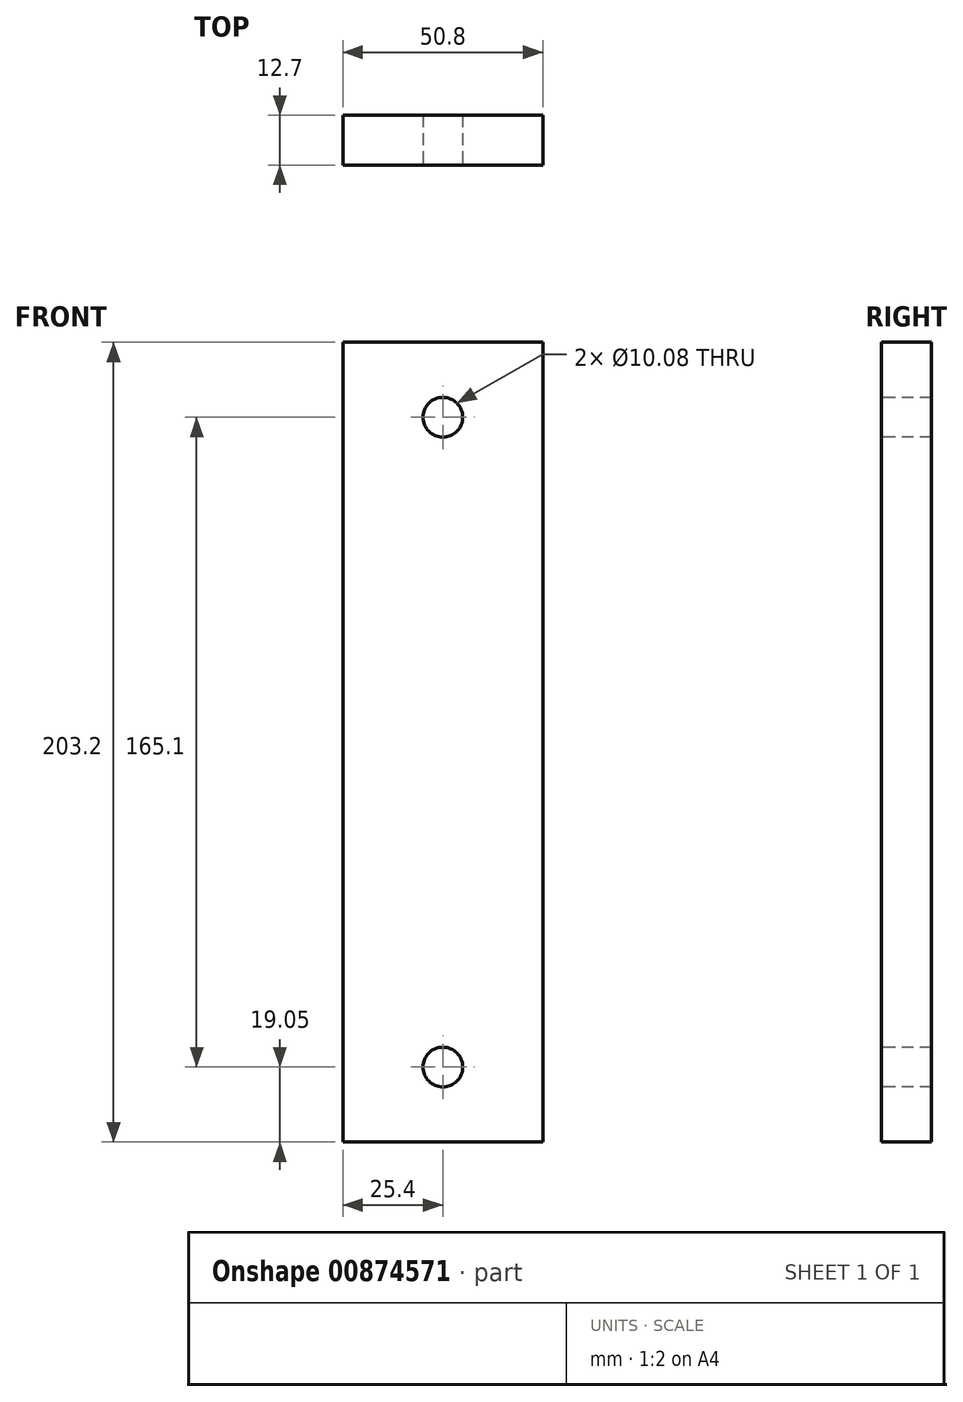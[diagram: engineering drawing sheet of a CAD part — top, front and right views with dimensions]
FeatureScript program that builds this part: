
annotation { "Feature Type Name" : "Feature", "Feature Type Description" : "" }
export const myFeature = defineFeature(function(context is Context, id is Id, definition is map)
    precondition{}
    {
        {
            var Q0;
            Q0=qCreatedBy(makeId("Front.planeOp"),FACE);
            var sketch = newSketch(context, id + "F0", { "sketchPlane" : qUnion([Q0])});
            skLineSegment(sketch, "E0.bottom", {"start": v(-25.4, 101.6) * mm, "end": v(25.4, 101.6) * mm});
            skLineSegment(sketch, "E0.top", {"start": v(-25.4, -101.6) * mm, "end": v(25.4, -101.6) * mm});
            skLineSegment(sketch, "E0.left", {"start": v(-25.4, 101.6) * mm, "end": v(-25.4, -101.6) * mm});
            skLineSegment(sketch, "E0.right", {"start": v(25.4, 101.6) * mm, "end": v(25.4, -101.6) * mm});
            skPoint(sketch, "E0.middle", {"position": v(0, 0) * mm});
            skPoint(sketch, "E1", {"position": v(0, 82.55) * mm});
            skPoint(sketch, "E1.positionSnap0", {"position": v(0, 101.6) * mm});
            skPoint(sketch, "E2", {"position": v(0, -82.55) * mm});
            skSolve(sketch);
        }
        {
            var Q0;
            Q0 = qSketchRegion(id + "F0", true);
            extrude(context, id + "F1", {"entities" : qUnion([Q0]), "depth" : 12.7 * mm, "offsetDistance" : 25.4 * mm});
        }
        {
            var Q0;
            Q0=sQuery(id+"F0.wireOp",VERTEX,"E1");
            var Q1;
            Q1=sQuery(id+"F0.wireOp",VERTEX,"E2");
            var Q2;
            Q2=makeQuery(id+"F1.opExtrude","SWEPT_BODY",BODY,{"disambiguationData":[OSD([sQuery(id+"F0.wireOp",EDGE,"E0.bottom"),sQuery(id+"F0.wireOp",EDGE,"E0.top"),sQuery(id+"F0.wireOp",EDGE,"E0.left"),sQuery(id+"F0.wireOp",EDGE,"E0.right")])]});
            hole(context, id + "F2", {"style" : HoleStyle.SIMPLE, "endStyle" : HoleEndStyle.BLIND, "oppositeDirection" : true, "standardTappedOrClearance" : lookupTablePath({ "fit" : "Normal (ASME)", "standard" : "ANSI", "size" : "3/8", "type" : "Clearance" }), "standardBlindInLast" : lookupTablePath({ "fit" : "Free", "standard" : "ANSI", "size" : "3/8", "type" : "Clearance" }), "holeDiameter" : 10.08 * mm, "majorDiameter" : 6.35 * mm, "holeDepth" : 12.7 * mm, "isTappedThrough" : true, "tappedDepth" : 10.34 * mm, "tapClearance" : 3, "locations" : qUnion([Q0, Q1]), "scope" : qUnion([Q2]), "startStyle" : HoleStartStyle.SKETCH});
        }
    });
